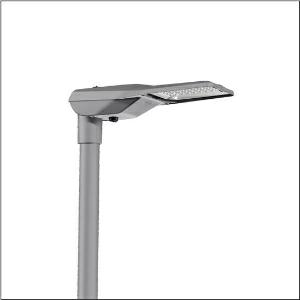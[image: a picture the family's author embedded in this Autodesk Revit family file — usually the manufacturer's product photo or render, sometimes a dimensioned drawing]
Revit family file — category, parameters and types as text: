
# Revit family: streetlight_sl_21_iq_mini___stw1_0a_5xe2e31y08gb_7efe
name_source: partatom
category: Lighting Fixtures
units: mm (PartAtom-declared; Revit-internal decimal feet)

## family parameters
Cut with Voids When Loaded = No
Host = Face
Light Source = No
Part Type = Normal
Room Calculation Point = No
Round Connector Dimension = Use Diameter
Shared = No

## types (1)
- --- (1 x LED, 5990 lm, 39.8 W, 3000K)
    Apparent Load = 40 VA
    CIE Flux Codes = 38 75 98 100 100
    Color Rendering = 70
    Color Temperature = 3000K
    Default Elevation = 1800 mm
    Description = Streetlight SL 21 iQ mini, mast luminaire, primary light control with lens, of PMMA, primary optical cover: cover, of toughened safety glass, transparent, light distribution: STW1.0a, light emission: direct distribution, primary light characteristic: asymmetric, installation type: post-top, side-entry, LED, High Power LED, rated luminous flux: 5.990lm, luminous efficacy: 151lm/W, light colour: 730, colour temperature: 3000K, control: presetting dimming logarithmic, Street-Remote, Auto-Match, Temp-Guard, Lumen-Switch, Night-Set, Smart-Wire, Light-Fading, Desk-Remote (wireless, voltage-free reading and setting of iQ features in the workshop via application-optimized NFC function/RFID function), optimised constant luminous flux control (CLO 2.0), mains connection: 220..240V, AC, 50/60Hz, start of lifetime: 40W, end of service life: 41W, reduction: 18W, luminaire housing, of diecast aluminium, powder-coated, Siteco® metallic grey (DB 702S), corrosivity category C5 mid according to DIN EN ISO 12944, please order mast flange separately, inclination adjustable: 0°, 5°, 10°, 15°, sealing non-destructively replaceable, multi-level sealing system, length: 628mm, width: 235mm, height: 110mm, mast flange for spigot size: 42mm (side-entry): 5XC10008XM4, 60/48mm (side-entry/post-top): 5XC10108XM2, 76/60mm (side-entry/post-top): 5XC10108XM1, Smart Interface below and above, protection rating (complete): IP66, insulation class (complete): insulation class II (safety insulation), certification: CE, ENEC, ENEC+, VDE, impact resistance: IK09, permissible operating ambient temperature for outdoor applications: -40..+50°C, standard-compliant lighting for roads and squares, packaging unit: 1 piece

Light Distribution: STW1.0a
    Height = 110 mm
    Lamp = 1 x LED
    Lamp Light Flux = 5990 lm
    Lamp Power = 39.8 W
    Lamp count = 1
    Length = 625 mm
    Luminous efficacy = 151 lm/W
    Manufacturer = Siteco
    ModVariant = No
    Model = 5XE2E31Y08GB
    Number of Poles = 1
    OnlyDefault = Yes
    Power Factor = 1
    Product Name = Streetlight SL 21 iQ mini | STW1.0a
    Product group = mast luminaire | pylon top
    ProductGroupID = 6100
    Protection Class = Protection class II
    Protection Degree = IP 66
    RLX_Detail_Level = 1
    RLX_Emergency_Light_Flux = 0 lm
    RLX_Emergency_Type = 0
    RLX_Emergency_Type_DB = No
    RlxData = <blob elided: 92853 chars, md5=92d8e6d0>
    Socket = socket
    Standby Power = 0 W
    System Light Flux = 5990 lm
    System Power = 40 W
    Type Comments = factory setting: luminous flux: 100 % | dim-lin: 254 | 800 mA
    Type Image = l_1003514.jpg
    URL = http://relux.com
    VarID = @adj_044377
    Voltage = 0 V
    Weight = 0.00 kg
    Width = 234 mm

## geometry (parser evidence)
native form markers: Blend x4, Sweep x12
no freeform markers — native parametric forms only
